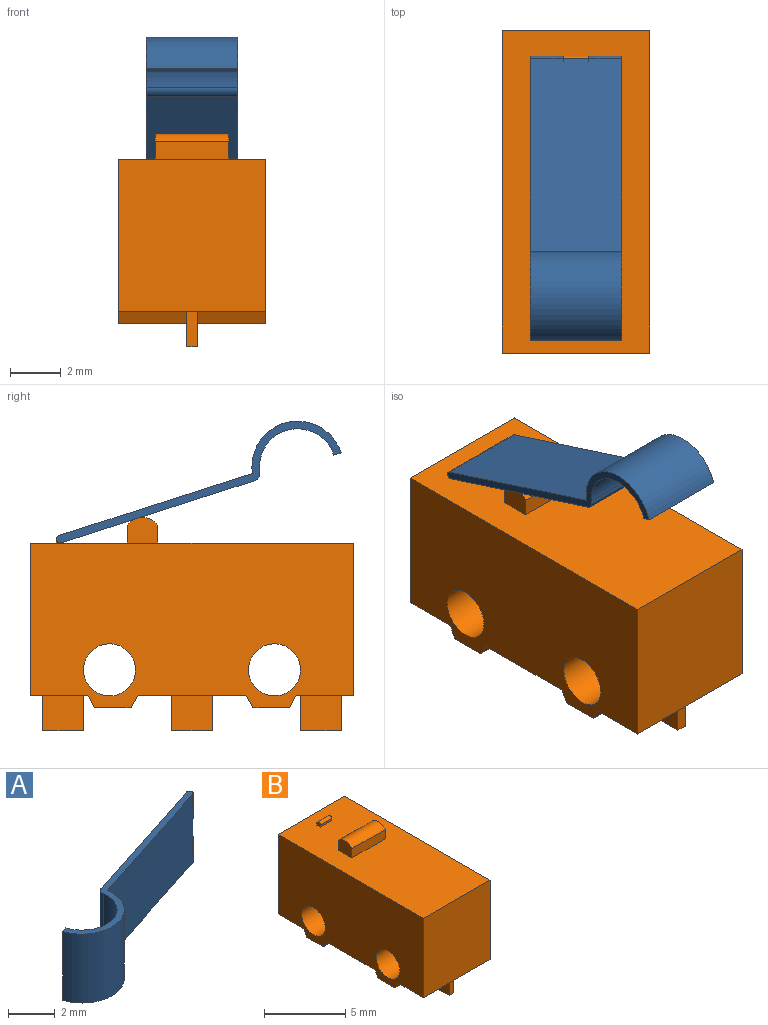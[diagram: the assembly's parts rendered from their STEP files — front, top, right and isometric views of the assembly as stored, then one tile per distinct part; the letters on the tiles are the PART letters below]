
ASSEMBLY  parts=2 mates=1
PART A: 17 faces, bbox 11.2x4.8x3.6 mm
  f0: cylinder r=0.15mm len=1.3mm, axis (0,0,1), area 0.6mm2, adj f2,f9,f11,f13
  f1: cylinder r=0.15mm len=1.3mm, axis (0,0,1), area 0.6mm2, adj f2,f9,f10,f12
  f2: plane 7.6x3.6mm, normal (-0.31,0.95,0), area 28.4mm2, adj f0,f1,f3,f10,f11,f12,f13,f14
  f3: plane 3.6x0mm, normal (-0.95,-0.31,0), area 0mm2, adj f2,f4,f10,f11
  f4: cylinder r=0.3mm len=3.6mm, axis (0,0,1), area 1.8mm2, adj f3,f5,f10,f11
  f5: plane 3.6x0.01mm, normal (-0.31,0.95,0), area 0mm2, adj f4,f6,f10,f11
  f6: cylinder r=1.5mm len=3.6mm, axis (0,0,1), area 15.9mm2, adj f5,f7,f10,f11
  f7: plane 3.6x0.29mm, normal (-0.31,0.95,0), area 1.1mm2, adj f6,f8,f10,f11
  f8: cylinder r=1.8mm len=3.6mm, axis (0,0,1), area 19.3mm2, adj f7,f9,f10,f11
  f9: plane 7.62x3.6mm, normal (0.31,-0.95,0), area 28.8mm2, adj f0,f1,f8,f10,f11,f15
  f10: plane 11.22x4.8mm, normal (0,0,1), area 4mm2, adj f1,f2,f3,f4,f5,f6,f7,f8
  f11: plane 11.22x4.8mm, normal (0,0,-1), area 4mm2, adj f0,f2,f3,f4,f5,f6,f7,f8
  f12: plane 0.3x0.3mm, normal (0,0,-1), area 0.1mm2, adj f1,f2,f14,f15
  f13: plane 0.3x0.3mm, normal (0,0,1), area 0.1mm2, adj f0,f2,f14,f15
  f14: plane 1x0.11mm, normal (1,0,0), area 0.1mm2, adj f2,f12,f13,f15
  f15: cylinder r=0.15mm len=1mm, axis (0,0,1), area 0.3mm2, adj f9,f12,f13,f14
  f16: cylinder r=0.75mm len=2.9mm, axis (0,0,1), area 0.2mm2, adj f2
PART B: 41 faces, bbox 5.8x12.7x8.4 mm
  f0: plane 2.9x0.7mm, normal (0,1,0), area 2mm2, adj f1,f3,f19,f20
  f1: plane 1.2x1mm, normal (-1,0,0), area 1.1mm2, adj f0,f2,f3,f20
  f2: plane 2.9x0.7mm, normal (0,-1,0), area 2mm2, adj f1,f3,f19,f20
  f3: plane 12.7x5.8mm, normal (0,0,1), area 69.9mm2, adj f0,f1,f2,f4,f5,f8,f9,f19
  f4: plane 6x5.8mm, normal (0,-1,0), area 34.8mm2, adj f3,f8,f9,f18
  f5: plane 6x5.8mm, normal (0,1,0), area 34.8mm2, adj f3,f8,f9,f12
  f6: plane 5.8x1.45mm, normal (0,0,-1), area 8.4mm2, adj f8,f9,f14,f17
  f7: plane 5.8x1.45mm, normal (0,0,-1), area 8.4mm2, adj f8,f9,f11,f13
  f8: plane 12.7x6.5mm, normal (-1,0,0), area 71.3mm2, adj f3,f4,f5,f6,f7,f10,f11,f12
  f9: plane 12.7x6.5mm, normal (1,0,0), area 71.3mm2, adj f3,f4,f5,f6,f7,f10,f11,f12
  f10: cylinder r=1.03mm len=5.8mm, axis (-1,0,0), area 37.4mm2, adj f8,f9
  f11: plane 5.8x0.5mm, normal (0,0.89,-0.45), area 3.2mm2, adj f7,f8,f9,f12
  f12: plane 5.8x2.25mm, normal (0,0,-1), area 12.4mm2, adj f5,f8,f9,f11,f26,f27,f28,f29
  f13: plane 5.8x0.5mm, normal (0,-0.88,-0.48), area 3.3mm2, adj f7,f8,f9,f15
  f14: plane 5.8x0.5mm, normal (0,0.88,-0.48), area 3.3mm2, adj f6,f8,f9,f15
  f15: plane 5.8x4.25mm, normal (0,0,-1), area 24mm2, adj f8,f9,f13,f14,f21,f22,f23,f24
  f16: cylinder r=1.03mm len=5.8mm, axis (-1,0,0), area 37.4mm2, adj f8,f9
  f17: plane 5.8x0.5mm, normal (0,-0.89,-0.45), area 3.2mm2, adj f6,f8,f9,f18
  f18: plane 5.8x2.25mm, normal (0,0,-1), area 12.4mm2, adj f4,f8,f9,f17,f31,f32,f33,f34
  f19: plane 1.2x1mm, normal (1,0,0), area 1.1mm2, adj f0,f2,f3,f20
  f20: cylinder r=0.75mm len=2.9mm, axis (-1,0,0), area 4mm2, adj f0,f1,f2,f19
  f21: plane 1.6x1.4mm, normal (-1,0,0), area 2.2mm2, adj f15,f22,f24,f25
  f22: plane 1.4x0.4mm, normal (0,1,0), area 0.6mm2, adj f15,f21,f23,f25
  f23: plane 1.6x1.4mm, normal (1,0,0), area 2.2mm2, adj f15,f22,f24,f25
  f24: plane 1.4x0.4mm, normal (0,-1,0), area 0.6mm2, adj f15,f21,f23,f25
  f25: plane 1.6x0.4mm, normal (0,0,-1), area 0.6mm2, adj f21,f22,f23,f24
  f26: plane 1.4x0.4mm, normal (0,1,0), area 0.6mm2, adj f12,f27,f29,f30
  f27: plane 1.6x1.4mm, normal (1,0,0), area 2.2mm2, adj f12,f26,f28,f30
  f28: plane 1.4x0.4mm, normal (0,-1,0), area 0.6mm2, adj f12,f27,f29,f30
  f29: plane 1.6x1.4mm, normal (-1,0,0), area 2.2mm2, adj f12,f26,f28,f30
  f30: plane 1.6x0.4mm, normal (0,0,-1), area 0.6mm2, adj f26,f27,f28,f29
  f31: plane 1.4x0.4mm, normal (0,1,0), area 0.6mm2, adj f18,f32,f34,f35
  f32: plane 1.6x1.4mm, normal (1,0,0), area 2.2mm2, adj f18,f31,f33,f35
  f33: plane 1.4x0.4mm, normal (0,-1,0), area 0.6mm2, adj f18,f32,f34,f35
  f34: plane 1.6x1.4mm, normal (-1,0,0), area 2.2mm2, adj f18,f31,f33,f35
  f35: plane 1.6x0.4mm, normal (0,0,-1), area 0.6mm2, adj f31,f32,f33,f34
  f36: plane 0.3x0.3mm, normal (1,0,0), area 0.1mm2, adj f3,f37,f39,f40
  f37: plane 1x0.15mm, normal (0,1,0), area 0.1mm2, adj f3,f36,f38,f40
  f38: plane 0.3x0.3mm, normal (-1,0,0), area 0.1mm2, adj f3,f37,f39,f40
  f39: plane 1x0.15mm, normal (0,-1,0), area 0.1mm2, adj f3,f36,f38,f40
  f40: cylinder r=0.15mm len=1mm, axis (-1,0,0), area 0.5mm2, adj f36,f37,f38,f39
PLACE A rot(axis=(-0.58,-0.58,0.58),120deg) t=(-6.08,5.37,6.42)mm
PLACE B t=(-5.58,0.17,-0.23)mm fixed
MATE revolute A.f15 <-> B.f40  axis (1,0,0) through (-6.08,5.37,6.42)mm
